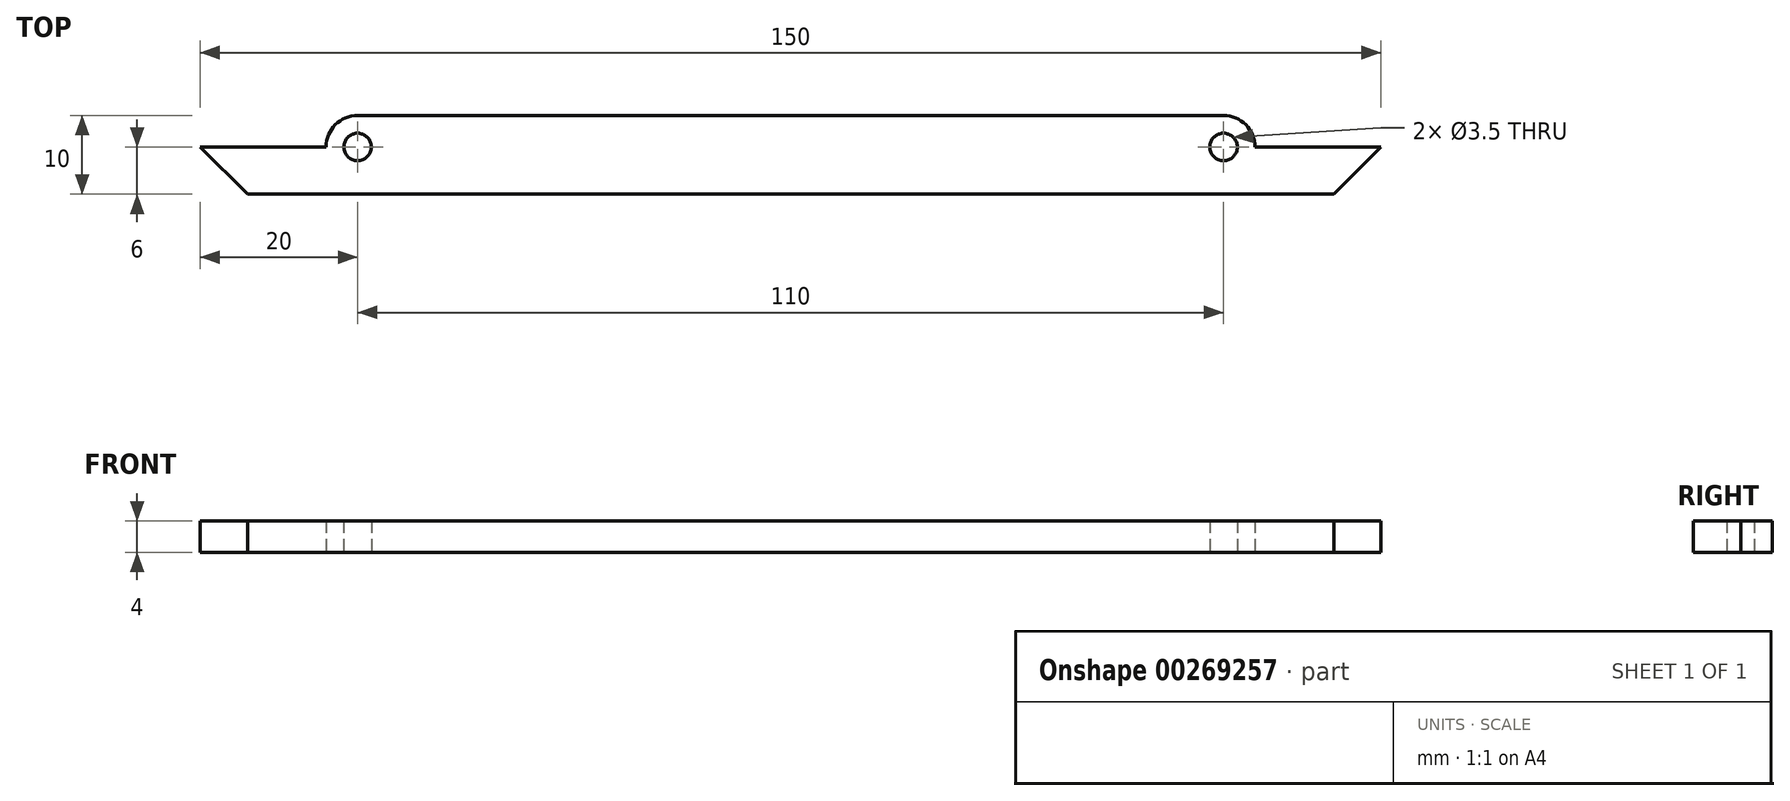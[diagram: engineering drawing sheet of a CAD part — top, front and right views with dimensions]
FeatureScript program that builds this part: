
annotation { "Feature Type Name" : "Feature", "Feature Type Description" : "" }
export const myFeature = defineFeature(function(context is Context, id is Id, definition is map)
    precondition{}
    {
        {
            var Q0;
            Q0=qCreatedBy(makeId("Top.planeOp"),FACE);
            var sketch = newSketch(context, id + "F0", { "sketchPlane" : qUnion([Q0])});
            skLineSegment(sketch, "E0", {"start": v(0, 0) * mm, "end": v(-51, 0) * mm});
            skLineSegment(sketch, "E1", {"start": v(0, 0) * mm, "end": v(51, 0) * mm});
            skLineSegment(sketch, "E2", {"start": v(75, 0) * mm, "end": v(59, 0) * mm});
            skLineSegment(sketch, "E3", {"start": v(-75, 0) * mm, "end": v(-59, 0) * mm});
            skCircle(sketch, "E4", {"center": v(-55, 0) * mm, "radius": 1.75 * mm});
            skCircle(sketch, "E5", {"center": v(55, 0) * mm, "radius": 1.75 * mm});
            skLineSegment(sketch, "E6", {"start": v(-75, 0) * mm, "end": v(-69, 0) * mm});
            skLineSegment(sketch, "E7", {"start": v(-69, -6) * mm, "end": v(-75, 0) * mm});
            skLineSegment(sketch, "E8", {"start": v(75, 0) * mm, "end": v(69, 0) * mm});
            skLineSegment(sketch, "E9", {"start": v(69, -6) * mm, "end": v(75, 0) * mm});
            skLineSegment(sketch, "E10", {"start": v(69, -6) * mm, "end": v(-69, -6) * mm});
            skCircle(sketch, "E11", {"center": v(-55, 0) * mm, "radius": 4 * mm});
            skArc(sketch, "E12", {"start": v(59, 0) * mm, "mid": v(55, 4) * mm, "end": v(51, 0) * mm});
            skLineSegment(sketch, "E13.trimOffspring", {"start": v(56.75, 0) * mm, "end": v(75, 0) * mm});
            skLineSegment(sketch, "E14.trimOffspring", {"start": v(-59, 0) * mm, "end": v(-75, 0) * mm});
            skSolve(sketch);
        }
        {
            var Q0;
            Q0 = qSketchRegion(id + "F0", true);
            extrude(context, id + "F1", {"entities" : qUnion([Q0]), "depth" : 4 * mm});
        }
        {
            var Q0;
            Q0=qCreatedBy(makeId("Top.planeOp"),FACE);
            var sketch = newSketch(context, id + "F2", { "sketchPlane" : qUnion([Q0])});
            skLineSegment(sketch, "E15", {"start": v(0, 0) * mm, "end": v(-53.25, 0) * mm});
            skLineSegment(sketch, "E16", {"start": v(0, 0) * mm, "end": v(53.25, 0) * mm});
            skLineSegment(sketch, "E17", {"start": v(55, 1.75) * mm, "end": v(55, 4) * mm});
            skLineSegment(sketch, "E18", {"start": v(55, 4) * mm, "end": v(-55, 4) * mm});
            skLineSegment(sketch, "E19", {"start": v(-55, 4) * mm, "end": v(-55, 1.75) * mm});
            skArc(sketch, "E20", {"start": v(-53.25, 0) * mm, "mid": v(-53.76, 1.24) * mm, "end": v(-55, 1.75) * mm});
            skArc(sketch, "E21", {"start": v(55, 1.75) * mm, "mid": v(53.76, 1.24) * mm, "end": v(53.25, 0) * mm});
            skSolve(sketch);
        }
        {
            var Q0;
            Q0 = qSketchRegion(id + "F2", true);
            extrude(context, id + "F3", {"entities" : qUnion([Q0]), "operationType" : NewBodyOperationType.ADD, "depth" : 4 * mm});
        }
    });
